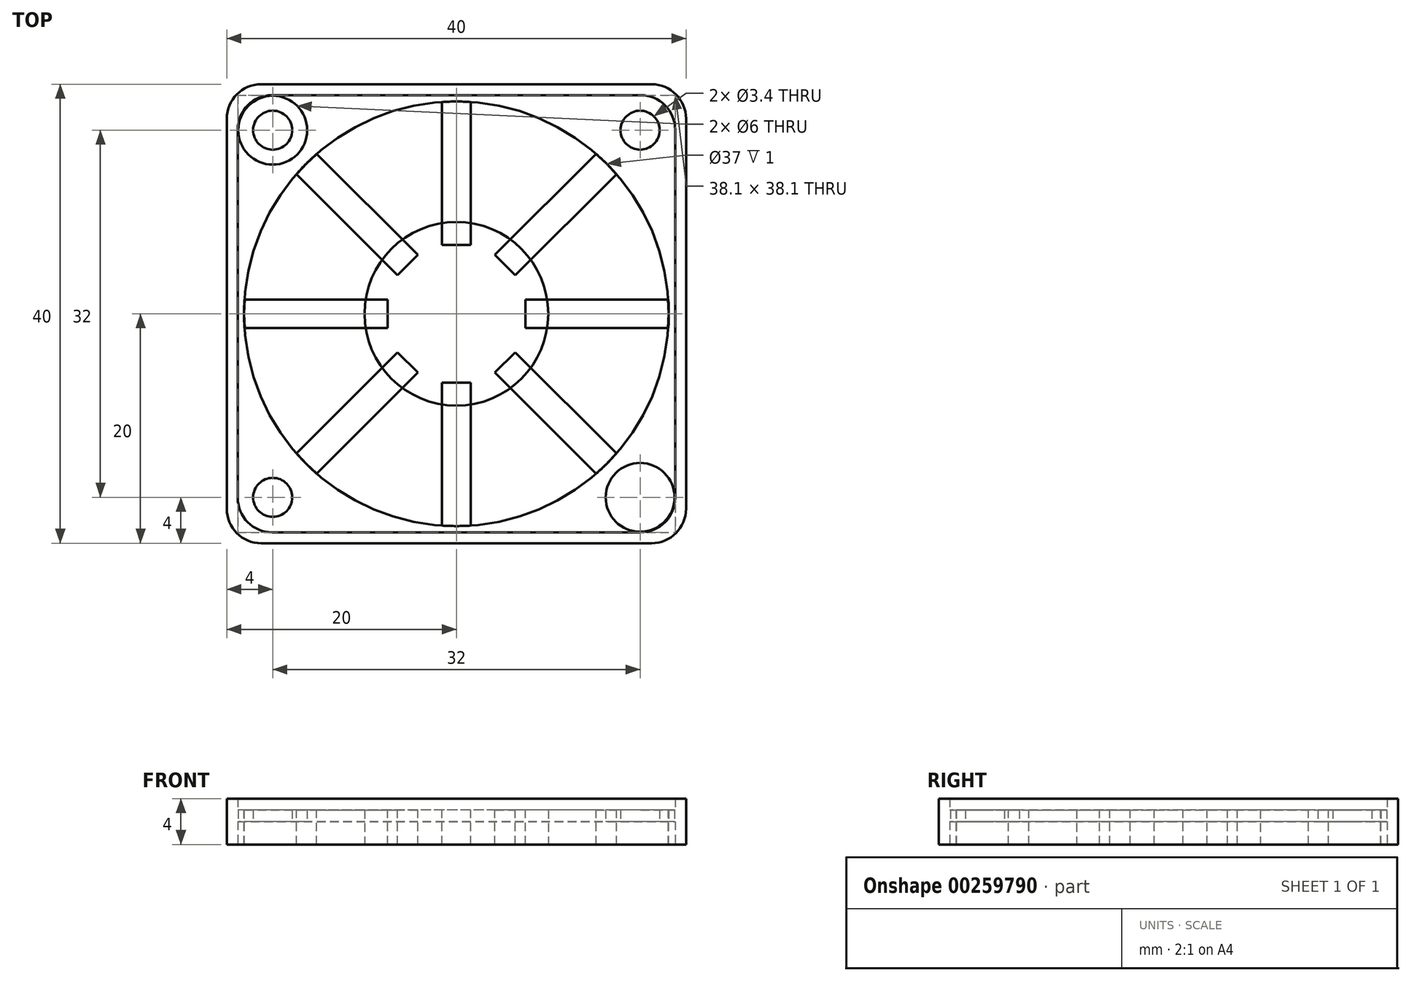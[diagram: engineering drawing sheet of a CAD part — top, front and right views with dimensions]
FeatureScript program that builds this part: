
annotation { "Feature Type Name" : "Feature", "Feature Type Description" : "" }
export const myFeature = defineFeature(function(context is Context, id is Id, definition is map)
    precondition{}
    {
        {
            var Q0;
            Q0=qCreatedBy(makeId("Top.planeOp"),FACE);
            var sketch = newSketch(context, id + "F0", { "sketchPlane" : qUnion([Q0])});
            skLineSegment(sketch, "E0.bottom", {"start": v(-20, 20) * mm, "end": v(20, 20) * mm});
            skLineSegment(sketch, "E0.top", {"start": v(-20, -20) * mm, "end": v(20, -20) * mm});
            skLineSegment(sketch, "E0.left", {"start": v(-20, 20) * mm, "end": v(-20, -20) * mm});
            skLineSegment(sketch, "E0.right", {"start": v(20, 20) * mm, "end": v(20, -20) * mm});
            skPoint(sketch, "E0.middle", {"position": v(0, 0) * mm});
            skCircle(sketch, "E1", {"center": v(0, 0) * mm, "radius": 8 * mm});
            skCircle(sketch, "E2", {"center": v(0, 0) * mm, "radius": 18.5 * mm});
            skLineSegment(sketch, "E3", {"start": v(20, 20) * mm, "end": v(-20, -20) * mm, "construction": true});
            skLineSegment(sketch, "E4", {"start": v(-20, 20) * mm, "end": v(20, -20) * mm, "construction": true});
            skCircle(sketch, "E5", {"center": v(16, 16) * mm, "radius": 3 * mm});
            skCircle(sketch, "E6", {"center": v(16, 16) * mm, "radius": 1.7 * mm});
            skCircle(sketch, "E7.MirrorC", {"center": v(-16, 16) * mm, "radius": 1.7 * mm});
            skCircle(sketch, "E8.MirrorC", {"center": v(-16, 16) * mm, "radius": 3 * mm});
            skCircle(sketch, "E9.MirrorC", {"center": v(16, -16) * mm, "radius": 3 * mm});
            skCircle(sketch, "E10.MirrorC", {"center": v(16, -16) * mm, "radius": 1.7 * mm});
            skCircle(sketch, "E11.MirrorC", {"center": v(-16, -16) * mm, "radius": 3 * mm});
            skCircle(sketch, "E12.MirrorC", {"center": v(-16, -16) * mm, "radius": 1.7 * mm});
            skLineSegment(sketch, "E13.bottom", {"start": v(-19.05, 19.05) * mm, "end": v(19.05, 19.05) * mm});
            skLineSegment(sketch, "E13.top", {"start": v(-19.05, -19.05) * mm, "end": v(19.05, -19.05) * mm});
            skLineSegment(sketch, "E13.left", {"start": v(-19.05, 19.05) * mm, "end": v(-19.05, -19.05) * mm});
            skLineSegment(sketch, "E13.right", {"start": v(19.05, 19.05) * mm, "end": v(19.05, -19.05) * mm});
            skSolve(sketch);
        }
        {
            var Q0;
            Q0=makeQuery(id+"F0.imprint","IMPRINT",FACE,{"disambiguationData":[TD([[makeQuery(id+"F0.imprint","IMPRINT",EDGE,{"derivedFrom":sQuery(id+"F0.wireOp",EDGE,"E2")}),-1.0]])]});
            var Q1;
            Q1=makeQuery(id+"F0.imprint","IMPRINT",FACE,{"disambiguationData":[TD([[makeQuery(id+"F0.imprint","IMPRINT",EDGE,{"derivedFrom":sQuery(id+"F0.wireOp",EDGE,"E7.MirrorC")}),1.0]])]});
            var Q2;
            Q2=makeQuery(id+"F0.imprint","IMPRINT",FACE,{"disambiguationData":[TD([[makeQuery(id+"F0.imprint","IMPRINT",EDGE,{"derivedFrom":sQuery(id+"F0.wireOp",EDGE,"E0.bottom")}),-1.0]])]});
            var Q3;
            Q3=makeQuery(id+"F0.imprint","IMPRINT",FACE,{"disambiguationData":[TD([[makeQuery(id+"F0.imprint","IMPRINT",EDGE,{"derivedFrom":sQuery(id+"F0.wireOp",EDGE,"E1")}),1.0]])]});
            var Q4;
            Q4=makeQuery(id+"F0.imprint","IMPRINT",FACE,{"disambiguationData":[TD([[makeQuery(id+"F0.imprint","IMPRINT",EDGE,{"derivedFrom":sQuery(id+"F0.wireOp",EDGE,"E11.MirrorC")}),1.0]])]});
            var Q5;
            Q5=makeQuery(id+"F0.imprint","IMPRINT",FACE,{"disambiguationData":[TD([[makeQuery(id+"F0.imprint","IMPRINT",EDGE,{"derivedFrom":sQuery(id+"F0.wireOp",EDGE,"E9.MirrorC")}),-1.0]])]});
            var Q6;
            Q6=makeQuery(id+"F0.imprint","IMPRINT",FACE,{"disambiguationData":[TD([[makeQuery(id+"F0.imprint","IMPRINT",EDGE,{"derivedFrom":sQuery(id+"F0.wireOp",EDGE,"E5")}),1.0]])]});
            extrude(context, id + "F1", {"entities" : qUnion([Q0, Q1, Q2, Q3, Q4, Q5, Q6]), "depth" : 3 * mm});
        }
        {
            var Q0;
            Q0=makeQuery(id+"F1.opExtrude","CAP_FACE",FACE,{"disambiguationData":[OSD([sQuery(id+"F0.wireOp",EDGE,"E0.bottom"),sQuery(id+"F0.wireOp",EDGE,"E0.top"),sQuery(id+"F0.wireOp",EDGE,"E0.left"),sQuery(id+"F0.wireOp",EDGE,"E0.right"),sQuery(id+"F0.wireOp",EDGE,"E2"),sQuery(id+"F0.wireOp",EDGE,"E5"),sQuery(id+"F0.wireOp",EDGE,"178JV0W0-UxBK-Eftk-ZxAv-Md0lSC3UNxa2"),sQuery(id+"F0.wireOp",EDGE,"9a6a856a-5fe4-4e18-bcab-08f5107acea00.MirrorC"),sQuery(id+"F0.wireOp",EDGE,"f4a2dd45-ac96-495a-a119-70c69025c0b60.MirrorC")])],"isStart":false});
            var sketch = newSketch(context, id + "F2", { "sketchPlane" : qUnion([Q0])});
            skLineSegment(sketch, "E14.bottom", {"start": v(1.25, 19) * mm, "end": v(-1.25, 19) * mm});
            skLineSegment(sketch, "E14.top", {"start": v(1.25, 6) * mm, "end": v(-1.25, 6) * mm});
            skLineSegment(sketch, "E14.left", {"start": v(1.25, 19) * mm, "end": v(1.25, 6) * mm});
            skLineSegment(sketch, "E14.right", {"start": v(-1.25, 19) * mm, "end": v(-1.25, 6) * mm});
            skPoint(sketch, "E14.middle", {"position": v(0, 12.5) * mm});
            skSolve(sketch);
        }
        {
            var Q0;
            {var subQ0=sQuery(id+"F2.wireOp",EDGE,"E14.top");Q0=makeQuery(id+"F2.imprint","IMPRINT",FACE,{"disambiguationData":[TD([[makeQuery(id+"F2.imprint","IMPRINT",EDGE,{"derivedFrom":subQ0}),-1.0]])]});}
            extrude(context, id + "F3", {"entities" : qUnion([Q0]), "oppositeDirection" : true, "depth" : 3 * mm});
        }
        {
            var Q0;
            Q0=qCreatedBy(makeId("Right.planeOp"),FACE);
            var sketch = newSketch(context, id + "F4", { "sketchPlane" : qUnion([Q0])});
            skLineSegment(sketch, "E15", {"start": v(0, 0) * mm, "end": v(0, 3) * mm});
            skSolve(sketch);
        }
        {
            var Q0;
            Q0=makeQuery(id+"F3.opExtrude","SWEPT_BODY",BODY,{"disambiguationData":[OSD([sQuery(id+"F0.wireOp",EDGE,"E2"),sQuery(id+"F2.wireOp",EDGE,"E14.top"),sQuery(id+"F2.wireOp",EDGE,"E14.left"),sQuery(id+"F2.wireOp",EDGE,"E14.right")])]});
            var Q1;
            Q1=sQuery(id+"F4.wireOp",EDGE,"E15");
            circularPattern(context, id + "F5", {"entities" : qUnion([Q0]), "axis" : qUnion([Q1]), "angle" : 360 * degree, "instanceCount" : 8, "equalSpace" : true});
        }
        {
            var Q0;
            Q0=makeQuery(id+"F0.imprint","IMPRINT",FACE,{"disambiguationData":[TD([[makeQuery(id+"F0.imprint","IMPRINT",EDGE,{"derivedFrom":sQuery(id+"F0.wireOp",EDGE,"E9.MirrorC")}),-1.0]])]});
            var Q1;
            Q1=makeQuery(id+"F0.imprint","IMPRINT",FACE,{"disambiguationData":[TD([[makeQuery(id+"F0.imprint","IMPRINT",EDGE,{"derivedFrom":sQuery(id+"F0.wireOp",EDGE,"E11.MirrorC")}),1.0]])]});
            var Q2;
            Q2=makeQuery(id+"F0.imprint","IMPRINT",FACE,{"disambiguationData":[TD([[makeQuery(id+"F0.imprint","IMPRINT",EDGE,{"derivedFrom":sQuery(id+"F0.wireOp",EDGE,"E7.MirrorC")}),1.0]])]});
            var Q3;
            Q3=makeQuery(id+"F0.imprint","IMPRINT",FACE,{"disambiguationData":[TD([[makeQuery(id+"F0.imprint","IMPRINT",EDGE,{"derivedFrom":sQuery(id+"F0.wireOp",EDGE,"E5")}),1.0]])]});
            extrude(context, id + "F6", {"entities" : qUnion([Q0, Q1, Q2, Q3]), "operationType" : NewBodyOperationType.REMOVE, "depth" : 2 * mm});
        }
        {
            var Q0;
            Q0=makeQuery(id+"F0.imprint","IMPRINT",FACE,{"disambiguationData":[TD([[makeQuery(id+"F0.imprint","IMPRINT",EDGE,{"derivedFrom":sQuery(id+"F0.wireOp",EDGE,"E0.bottom")}),-1.0]])]});
            extrude(context, id + "F7", {"entities" : qUnion([Q0]), "operationType" : NewBodyOperationType.ADD, "depth" : 4 * mm});
        }
        {
            var Q0;
            {var subQ0=sQuery(id+"F0.wireOp",EDGE,"E0.left");var subQ1=sQuery(id+"F0.wireOp",EDGE,"E0.top");Q0=makeQuery(id+"F7.boolean.opBoolean","MERGE",EDGE,{"derivedFrom":[makeQuery(id+"F1.opExtrude","SWEPT_EDGE",EDGE,{"disambiguationData":[OSD([subQ1,subQ0])]}),makeQuery(id+"F7.opExtrude","SWEPT_EDGE",EDGE,{"disambiguationData":[OSD([subQ1,subQ0])]})]});}
            var Q1;
            {var subQ0=sQuery(id+"F0.wireOp",EDGE,"E0.right");var subQ1=sQuery(id+"F0.wireOp",EDGE,"E0.top");Q1=makeQuery(id+"F7.boolean.opBoolean","MERGE",EDGE,{"derivedFrom":[makeQuery(id+"F1.opExtrude","SWEPT_EDGE",EDGE,{"disambiguationData":[OSD([subQ1,subQ0])]}),makeQuery(id+"F7.opExtrude","SWEPT_EDGE",EDGE,{"disambiguationData":[OSD([subQ1,subQ0])]})]});}
            var Q2;
            {var subQ0=sQuery(id+"F0.wireOp",EDGE,"E0.right");var subQ1=sQuery(id+"F0.wireOp",EDGE,"E0.bottom");Q2=makeQuery(id+"F7.boolean.opBoolean","MERGE",EDGE,{"derivedFrom":[makeQuery(id+"F1.opExtrude","SWEPT_EDGE",EDGE,{"disambiguationData":[OSD([subQ1,subQ0])]}),makeQuery(id+"F7.opExtrude","SWEPT_EDGE",EDGE,{"disambiguationData":[OSD([subQ1,subQ0])]})]});}
            var Q3;
            {var subQ0=sQuery(id+"F0.wireOp",EDGE,"E0.left");var subQ1=sQuery(id+"F0.wireOp",EDGE,"E0.bottom");Q3=makeQuery(id+"F7.boolean.opBoolean","MERGE",EDGE,{"derivedFrom":[makeQuery(id+"F1.opExtrude","SWEPT_EDGE",EDGE,{"disambiguationData":[OSD([subQ1,subQ0])]}),makeQuery(id+"F7.opExtrude","SWEPT_EDGE",EDGE,{"disambiguationData":[OSD([subQ1,subQ0])]})]});}
            fillet(context, id + "F8", {"entities" : qUnion([Q0, Q1, Q2, Q3]), "radius" : 3 * mm, "tangentPropagation" : true, "allowEdgeOverflow" : false});
        }
        {
            var Q0;
            Q0=makeQuery(id+"F7.opExtrude","SWEPT_EDGE",EDGE,{"disambiguationData":[OSD([sQuery(id+"F0.wireOp",EDGE,"E13.top"),sQuery(id+"F0.wireOp",EDGE,"E13.left")])]});
            var Q1;
            Q1=makeQuery(id+"F7.opExtrude","SWEPT_EDGE",EDGE,{"disambiguationData":[OSD([sQuery(id+"F0.wireOp",EDGE,"E13.bottom"),sQuery(id+"F0.wireOp",EDGE,"E13.left")])]});
            var Q2;
            Q2=makeQuery(id+"F7.opExtrude","SWEPT_EDGE",EDGE,{"disambiguationData":[OSD([sQuery(id+"F0.wireOp",EDGE,"E13.bottom"),sQuery(id+"F0.wireOp",EDGE,"E13.right")])]});
            var Q3;
            Q3=makeQuery(id+"F7.opExtrude","SWEPT_EDGE",EDGE,{"disambiguationData":[OSD([sQuery(id+"F0.wireOp",EDGE,"E13.top"),sQuery(id+"F0.wireOp",EDGE,"E13.right")])]});
            fillet(context, id + "F9", {"entities" : qUnion([Q0, Q1, Q2, Q3]), "radius" : 3 * mm, "tangentPropagation" : true, "allowEdgeOverflow" : false});
        }
    });
